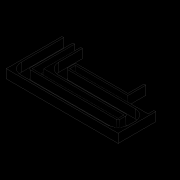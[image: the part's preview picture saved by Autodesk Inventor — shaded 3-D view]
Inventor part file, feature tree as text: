
AUTODESK INVENTOR PART (.ipt)
format: ipt  version: 2022 (Build 260153000, 153)  size: 192,000 bytes
history: native  units: in
note: dims shown in document units (in); Inventor stores cm internally (conversion verified against a paired STEP export)
features: fillet x2, extrude x1, sketch x1
ambient origin geometry x8: Origin, YZ Plane, XZ Plane, XY Plane, X Axis, Y Axis, Z Axis, Center Point
bodies: Solid1 (feature_tree)
feature tree (4):
  extrude  "Extrusion1"  Depth=1.378in
  fillet  "Fillet1"  Radius=0.1575in
  fillet  "Fillet2"  Radius=0.1575in
  sketch  "Sketch1"  dims[d10=4.7244in d13=1.378in d14=0.1575in d15=0.1575in d16=0.1575in d17=0.4921in d20=0.7874in d21=0.1575in d23=0.1575in d25=0.1575in d26=0.7874in d28=0.748in d29=0.0in d31=0.1575in d32=0.1575in d34=0.4921in d35=0.1575in d36=0.7874in d37=0.9449in d38=0.1575in d43=0.1575in d44=0.1575in d46=0.7874in d47=0.1575in d48=0.7874in d49=0.1575in d50=5.2362in d51=6.811in]
